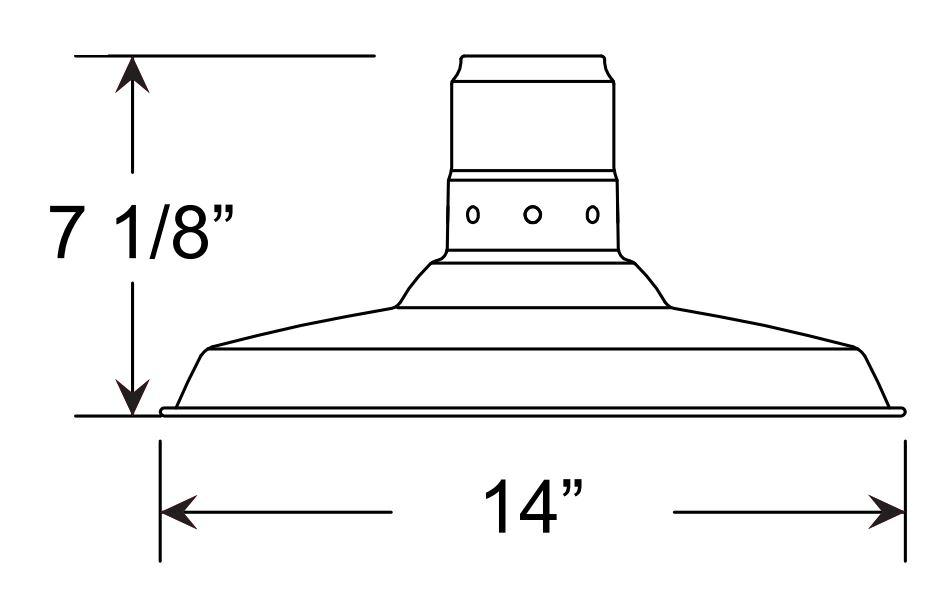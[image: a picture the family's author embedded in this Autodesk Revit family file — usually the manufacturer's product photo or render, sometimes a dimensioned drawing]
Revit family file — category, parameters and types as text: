
# Revit family: OSDDF Metal Fabric MB 22,30,36
name_source: partatom
category: Lighting Fixtures
units: mm (PartAtom-declared; Revit-internal decimal feet)

## family parameters
Always vertical = Yes
Cut with Voids When Loaded = No
Light Source = Yes
OmniClass Number = 23.80.70.00
OmniClass Title = Lighting
Part Type = Normal
Room Calculation Point = No
Round Connector Dimension = Use Diameter
Shared = No
Work Plane-Based = No

## types (3) — shared parameters
Apparent Load = 200 VA
Body Colour = Spun aluminium
Body Material = body
Bulb = Glass
CRI = >90
Canopy Body = GY
Color Filter = 16777215
Construction Material = Heavy Duty spun aluminum.
Default Elevation = 0' - 0"
Description = 120-277 Voltage
Dimming = 1%
Dimming Lamp Color Temperature Shift = <None>
Efficiency = 65-125 lumens per watt
HUB = Texture Black
Lamp = MB
Life = L70 50,000 hours
Load Classification = Lighting
Manufacturer = ANP Lighting
Photometric Web File = generic
Power Factor = 1
Tilt Angle = 90.00°
URL = https://www.anplighting.com
Voltage = 120 V
Warranty = 5 year limited warranty
b = 0' - 3"

## per-type parameters (varying)
| type | Fixture Diameter | Fixture Height | OSDDF22 | OSDDF30 | OSDDF36 | Wattage Comments | Weight | a |
| OSDDF22 | 1' - 10" | 1' - 1" | Yes | No | No | 200 W | 13.0 lbs | 1' - 1" |
| OSDDF30 | 2' - 6" | 1' - 5 1/2" | No | Yes | No | 200W | 10.5 lbs | 1' - 6" |
| OSDDF36 | 3' - 0" | 1' - 9" | No | No | Yes | 200W | 11.5 lbs | 1' - 8" |

note: column(s) folded — value = type name in every type: Model

## geometry (parser evidence)
native form markers: Sweep x44
no freeform markers — native parametric forms only
